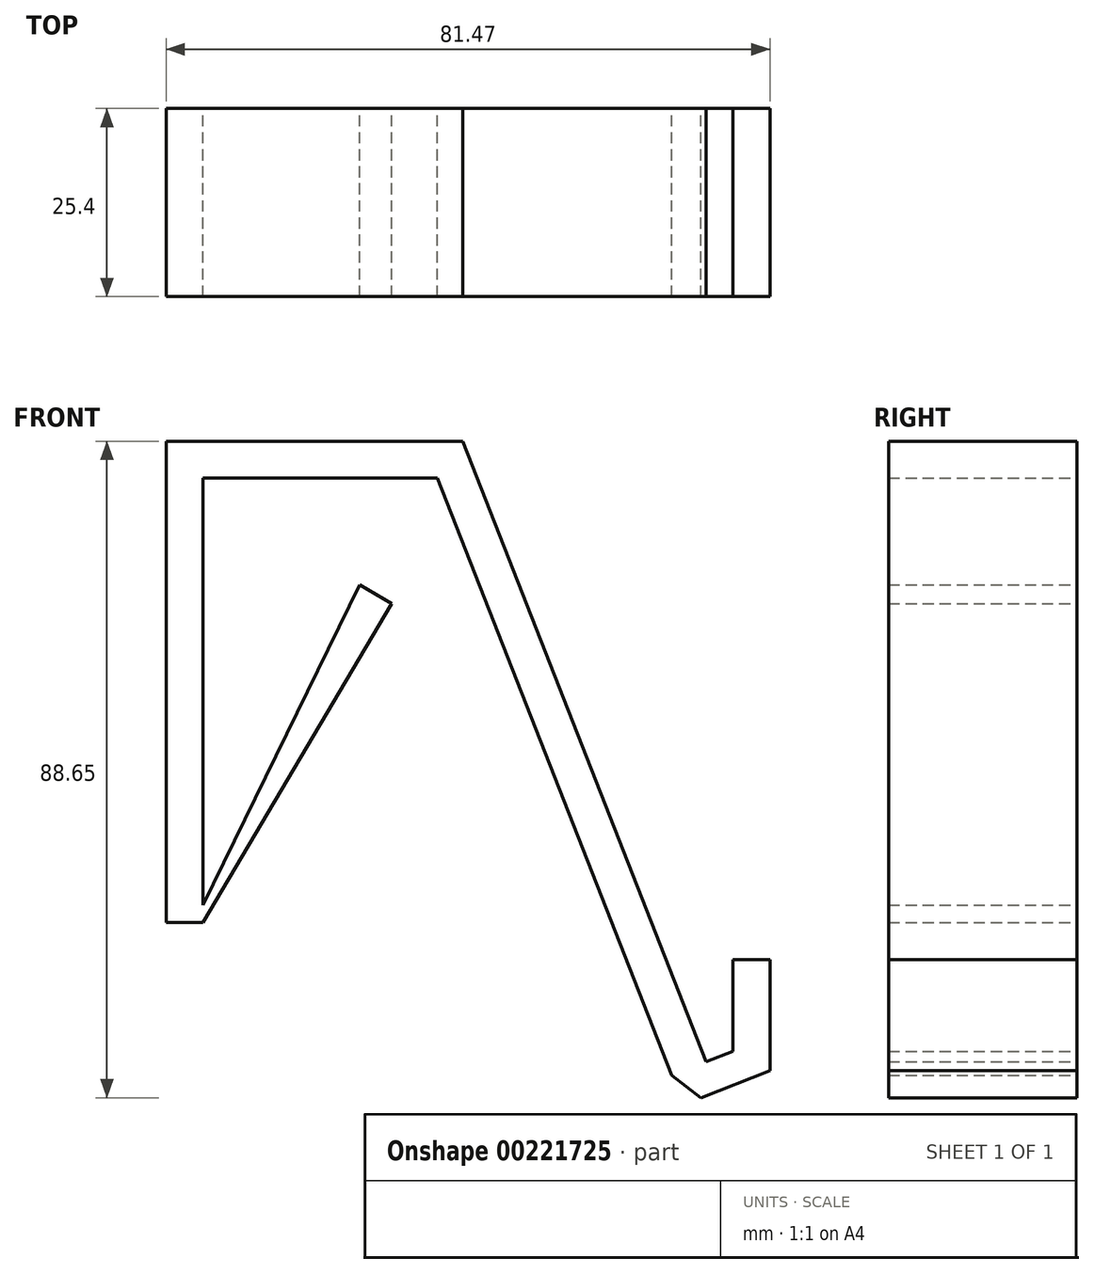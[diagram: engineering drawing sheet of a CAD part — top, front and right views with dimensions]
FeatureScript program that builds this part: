
annotation { "Feature Type Name" : "Feature", "Feature Type Description" : "" }
export const myFeature = defineFeature(function(context is Context, id is Id, definition is map)
    precondition{}
    {
        {
            var Q0;
            Q0=qCreatedBy(makeId("Front.planeOp"),FACE);
            var sketch = newSketch(context, id + "F0", { "sketchPlane" : qUnion([Q0])});
            skLineSegment(sketch, "E0", {"start": v(-70.27, 43.57) * mm, "end": v(-70.27, -16.43) * mm});
            skLineSegment(sketch, "E1", {"start": v(-70.27, -16.43) * mm, "end": v(-65.27, -16.43) * mm});
            skLineSegment(sketch, "E2", {"start": v(-65.27, -16.43) * mm, "end": v(-65.27, 43.57) * mm});
            skLineSegment(sketch, "E3", {"start": v(-65.27, 43.57) * mm, "end": v(-70.27, 43.57) * mm});
            skLineSegment(sketch, "E4", {"start": v(-65.27, -16.43) * mm, "end": v(-39.85, 26.62) * mm});
            skLineSegment(sketch, "E5", {"start": v(-39.85, 26.62) * mm, "end": v(-44.15, 29.17) * mm});
            skLineSegment(sketch, "E6", {"start": v(-44.15, 29.17) * mm, "end": v(-65.27, -14.05) * mm});
            skLineSegment(sketch, "E7", {"start": v(-70.27, 43.57) * mm, "end": v(-70.27, 48.57) * mm});
            skLineSegment(sketch, "E8", {"start": v(-70.27, 48.57) * mm, "end": v(-30.27, 48.57) * mm});
            skLineSegment(sketch, "E9", {"start": v(-30.27, 48.57) * mm, "end": v(-30.27, 43.57) * mm});
            skLineSegment(sketch, "E10", {"start": v(-65.27, 43.57) * mm, "end": v(-30.27, 43.57) * mm});
            skLineSegment(sketch, "E11", {"start": v(-30.27, 48.57) * mm, "end": v(2.57, -35.23) * mm});
            skLineSegment(sketch, "E12", {"start": v(2.57, -35.23) * mm, "end": v(-2.09, -37.05) * mm});
            skLineSegment(sketch, "E13", {"start": v(-2.09, -37.05) * mm, "end": v(-33.68, 43.57) * mm});
            skLineSegment(sketch, "E14", {"start": v(-2.09, -37.05) * mm, "end": v(1.89, -40.08) * mm});
            skLineSegment(sketch, "E15", {"start": v(1.89, -40.08) * mm, "end": v(11.2, -36.44) * mm});
            skLineSegment(sketch, "E16", {"start": v(11.2, -36.44) * mm, "end": v(11.2, -21.44) * mm});
            skLineSegment(sketch, "E17", {"start": v(11.2, -21.44) * mm, "end": v(6.2, -21.44) * mm});
            skLineSegment(sketch, "E18", {"start": v(6.2, -21.44) * mm, "end": v(6.2, -33.8) * mm});
            skLineSegment(sketch, "E19", {"start": v(6.2, -33.8) * mm, "end": v(2.57, -35.23) * mm});
            skSolve(sketch);
        }
        {
            var Q0;
            Q0 = qSketchRegion(id + "F0", true);
            extrude(context, id + "F1", {"entities" : qUnion([Q0]), "depth" : 25.4 * mm});
        }
    });
